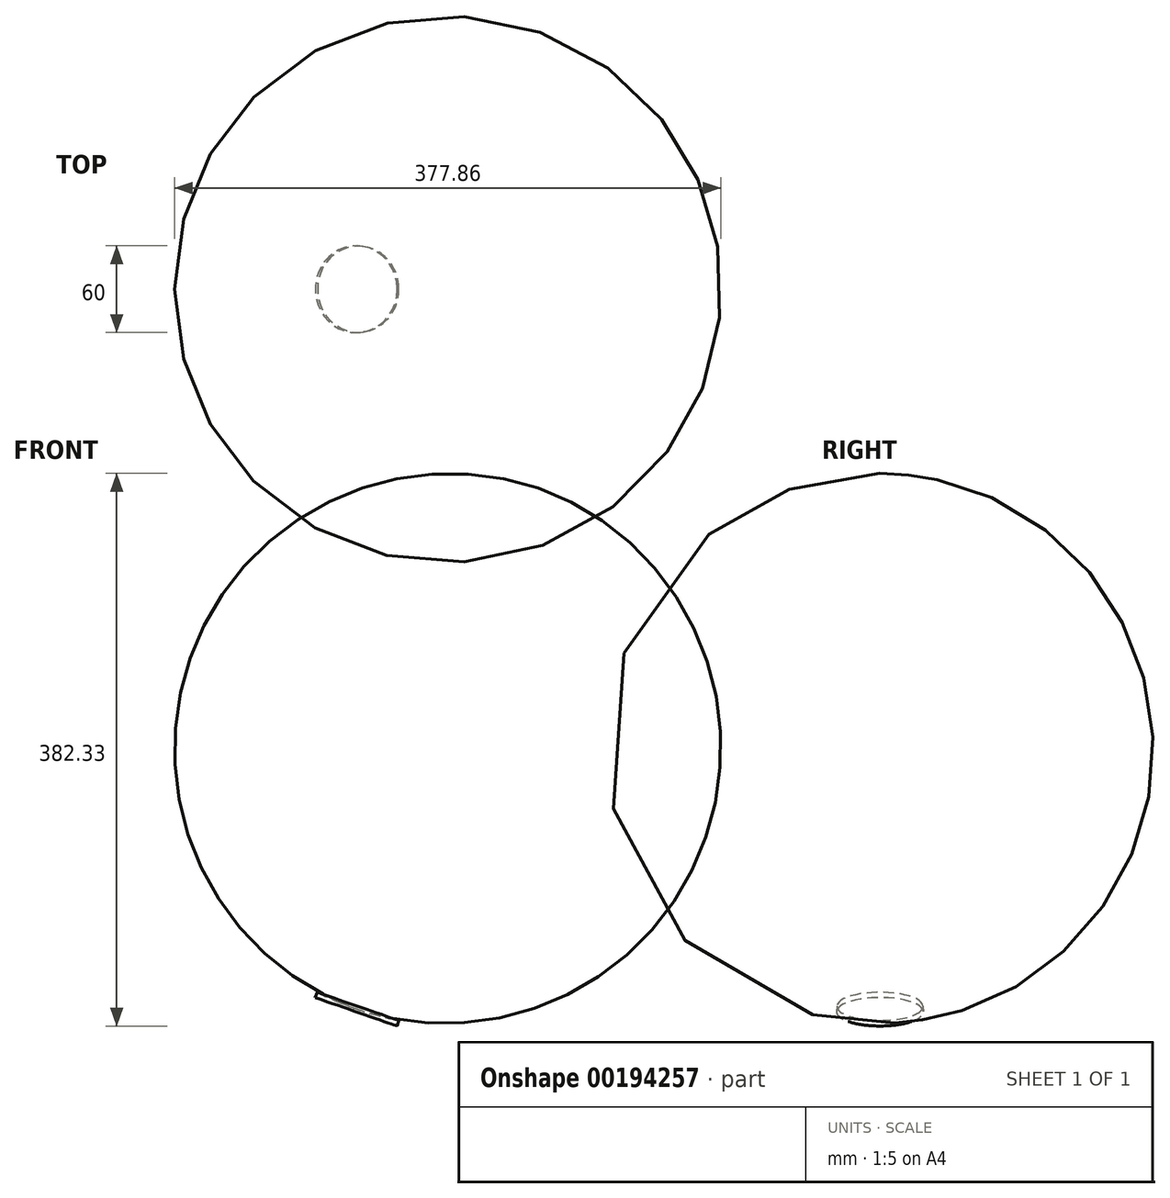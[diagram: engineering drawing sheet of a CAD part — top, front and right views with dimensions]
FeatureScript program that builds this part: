
annotation { "Feature Type Name" : "Feature", "Feature Type Description" : "" }
export const myFeature = defineFeature(function(context is Context, id is Id, definition is map)
    precondition{}
    {
        {
            var Q0;
            Q0=qCreatedBy(makeId("Front.planeOp"),FACE);
            var sketch = newSketch(context, id + "F0", { "sketchPlane" : qUnion([Q0])});
            skPoint(sketch, "E0.0", {"position": v(13.75, -6.3) * mm});
            skPoint(sketch, "E1.0", {"position": v(14.83, -2.45) * mm});
            skPoint(sketch, "E2.0", {"position": v(-14.6, 3.53) * mm});
            skPoint(sketch, "E3.0", {"position": v(-13.94, 5.42) * mm});
            skLineSegment(sketch, "E4", {"start": v(-14.6, 3.53) * mm, "end": v(13.75, -6.3) * mm});
            skLineSegment(sketch, "E5", {"start": v(13.75, -6.3) * mm, "end": v(14.83, -2.45) * mm});
            skLineSegment(sketch, "E6", {"start": v(-13.94, 5.42) * mm, "end": v(-14.6, 3.53) * mm});
            skArc(sketch, "E7", {"start": v(-13.94, 5.42) * mm, "mid": v(0.3, 0.92) * mm, "end": v(14.83, -2.45) * mm});
            skSolve(sketch);
        }
        {
            var Q0;
            Q0=makeQuery(id+"F0.imprint","IMPRINT",FACE,{"disambiguationData":[TD([[makeQuery(id+"F0.imprint","IMPRINT",EDGE,{"derivedFrom":sQuery(id+"F0.wireOp",EDGE,"E4")}),1.0]])]});
            var Q1;
            Q1=sQuery(id+"F0.wireOp",EDGE,"E6");
            revolve(context, id + "F1", {"entities" : qUnion([Q0]), "axis" : qUnion([Q1]), "revolveType" : RevolveType.FULL});
        }
    });
